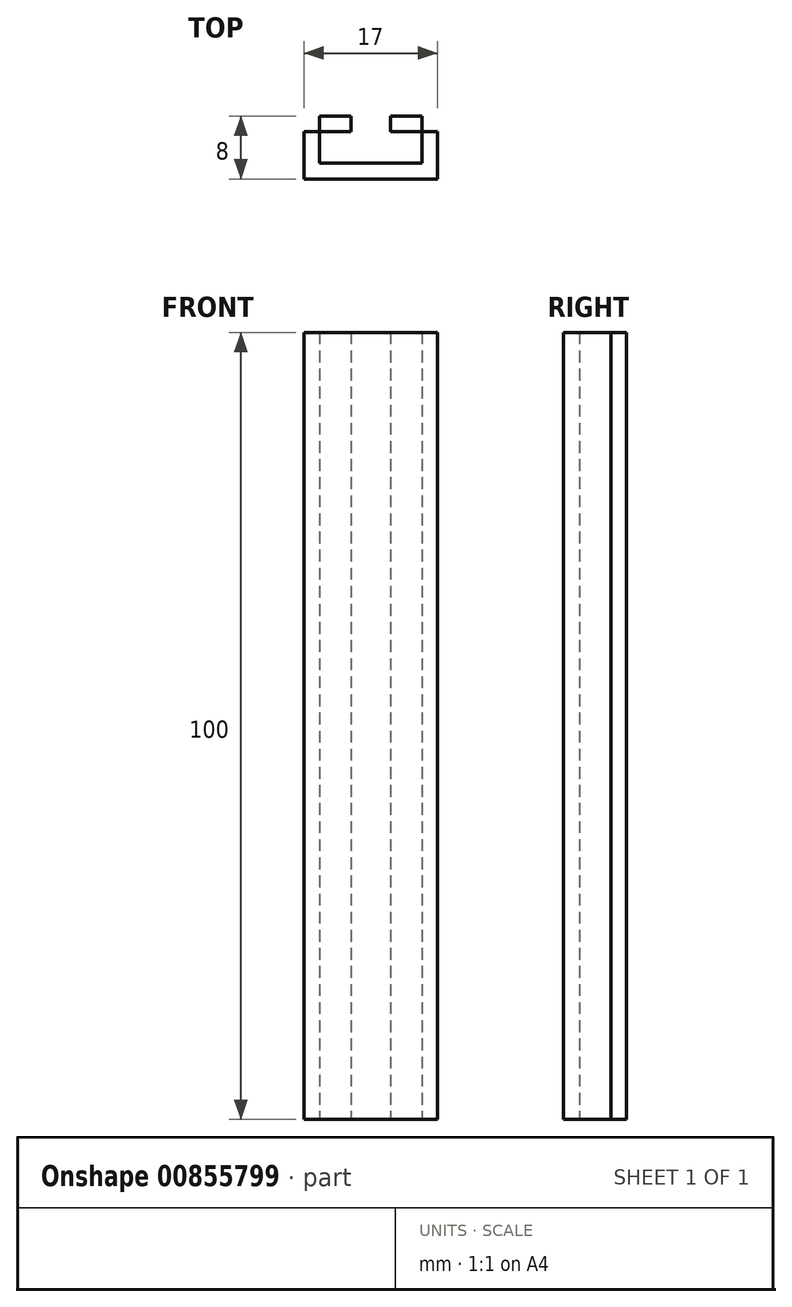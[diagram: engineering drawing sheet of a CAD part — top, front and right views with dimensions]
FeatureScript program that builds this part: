
annotation { "Feature Type Name" : "Feature", "Feature Type Description" : "" }
export const myFeature = defineFeature(function(context is Context, id is Id, definition is map)
    precondition{}
    {
        {
            var Q0;
            Q0=qCreatedBy(makeId("Top.planeOp"),FACE);
            var sketch = newSketch(context, id + "F0", { "sketchPlane" : qUnion([Q0])});
            skLineSegment(sketch, "E0.bottom", {"start": v(0, 0) * mm, "end": v(-8.5, 0) * mm});
            skLineSegment(sketch, "E0.top", {"start": v(0, 2) * mm, "end": v(-8.5, 2) * mm});
            skLineSegment(sketch, "E0.left", {"start": v(0, 0) * mm, "end": v(0, 2) * mm});
            skLineSegment(sketch, "E0.right", {"start": v(-8.5, 0) * mm, "end": v(-8.5, 2) * mm});
            skLineSegment(sketch, "E1.bottom", {"start": v(0, 0) * mm, "end": v(8.5, 0) * mm});
            skLineSegment(sketch, "E1.top", {"start": v(0, 2) * mm, "end": v(8.5, 2) * mm});
            skLineSegment(sketch, "E1.right", {"start": v(8.5, 0) * mm, "end": v(8.5, 2) * mm});
            skLineSegment(sketch, "E2.bottom", {"start": v(-8.5, 0) * mm, "end": v(-6.5, 0) * mm});
            skLineSegment(sketch, "E2.top", {"start": v(-8.5, 8) * mm, "end": v(-6.5, 8) * mm});
            skLineSegment(sketch, "E2.left", {"start": v(-8.5, 0) * mm, "end": v(-8.5, 8) * mm});
            skLineSegment(sketch, "E2.right", {"start": v(-6.5, 0) * mm, "end": v(-6.5, 8) * mm});
            skLineSegment(sketch, "E3.bottom", {"start": v(8.5, 0) * mm, "end": v(6.5, 0) * mm});
            skLineSegment(sketch, "E3.top", {"start": v(8.5, 8) * mm, "end": v(6.5, 8) * mm});
            skLineSegment(sketch, "E3.left", {"start": v(8.5, 0) * mm, "end": v(8.5, 8) * mm});
            skLineSegment(sketch, "E3.right", {"start": v(6.5, 0) * mm, "end": v(6.5, 8) * mm});
            skLineSegment(sketch, "E4.bottom", {"start": v(-8.5, 8) * mm, "end": v(-2.5, 8) * mm});
            skLineSegment(sketch, "E4.top", {"start": v(-8.5, 6) * mm, "end": v(-2.5, 6) * mm});
            skLineSegment(sketch, "E4.left", {"start": v(-8.5, 8) * mm, "end": v(-8.5, 6) * mm});
            skLineSegment(sketch, "E4.right", {"start": v(-2.5, 8) * mm, "end": v(-2.5, 6) * mm});
            skLineSegment(sketch, "E5.bottom", {"start": v(8.5, 8) * mm, "end": v(2.5, 8) * mm});
            skLineSegment(sketch, "E5.top", {"start": v(8.5, 6) * mm, "end": v(2.5, 6) * mm});
            skLineSegment(sketch, "E5.left", {"start": v(8.5, 8) * mm, "end": v(8.5, 6) * mm});
            skLineSegment(sketch, "E5.right", {"start": v(2.5, 8) * mm, "end": v(2.5, 6) * mm});
            skSolve(sketch);
        }
        {
            var Q0;
            {var subQ5=sQuery(id+"F0.wireOp",EDGE,"E4.right");Q0=makeQuery(id+"F0.imprint","IMPRINT",FACE,{"disambiguationData":[TD([[makeQuery(id+"F0.imprint","IMPRINT",EDGE,{"derivedFrom":subQ5}),-1.0]])]});}
            var Q1;
            {var subQ5=sQuery(id+"F0.wireOp",EDGE,"E4.left");Q1=makeQuery(id+"F0.imprint","IMPRINT",FACE,{"disambiguationData":[TD([[makeQuery(id+"F0.imprint","IMPRINT",EDGE,{"derivedFrom":subQ5}),1.0]])]});}
            var Q2;
            {var subQ0=sQuery(id+"F0.wireOp",EDGE,"E2.left");var subQ1=sQuery(id+"F0.wireOp",EDGE,"E0.top");var subQ2=makeQuery(id+"F0.imprint","INTERSECT",VERTEX,{"derivedFrom":[subQ1,subQ0]});Q2=makeQuery(id+"F0.imprint","IMPRINT",FACE,{"disambiguationData":[TD([[makeQuery(id+"F0.imprint","IMPRINT",EDGE,{"disambiguationData":[TD([[subQ2,1.0]])],"derivedFrom":subQ1}),-1.0]])]});}
            var Q3;
            {var subQ5=sQuery(id+"F0.wireOp",EDGE,"E2.bottom");Q3=makeQuery(id+"F0.imprint","IMPRINT",FACE,{"disambiguationData":[TD([[makeQuery(id+"F0.imprint","IMPRINT",EDGE,{"derivedFrom":subQ5}),1.0]])]});}
            var Q4;
            {var subQ0=sQuery(id+"F0.wireOp",EDGE,"E0.bottom");Q4=makeQuery(id+"F0.imprint","IMPRINT",FACE,{"disambiguationData":[TD([[makeQuery(id+"F0.imprint","IMPRINT",EDGE,{"derivedFrom":subQ0}),-1.0]])]});}
            var Q5;
            {var subQ0=sQuery(id+"F0.wireOp",EDGE,"E1.bottom");Q5=makeQuery(id+"F0.imprint","IMPRINT",FACE,{"disambiguationData":[TD([[makeQuery(id+"F0.imprint","IMPRINT",EDGE,{"derivedFrom":subQ0}),1.0]])]});}
            var Q6;
            {var subQ5=sQuery(id+"F0.wireOp",EDGE,"E3.bottom");Q6=makeQuery(id+"F0.imprint","IMPRINT",FACE,{"disambiguationData":[TD([[makeQuery(id+"F0.imprint","IMPRINT",EDGE,{"derivedFrom":subQ5}),-1.0]])]});}
            var Q7;
            {var subQ0=sQuery(id+"F0.wireOp",EDGE,"E3.left");var subQ1=sQuery(id+"F0.wireOp",EDGE,"E1.top");var subQ2=makeQuery(id+"F0.imprint","INTERSECT",VERTEX,{"derivedFrom":[subQ1,subQ0]});Q7=makeQuery(id+"F0.imprint","IMPRINT",FACE,{"disambiguationData":[TD([[makeQuery(id+"F0.imprint","IMPRINT",EDGE,{"disambiguationData":[TD([[subQ2,1.0]])],"derivedFrom":subQ1}),1.0]])]});}
            var Q8;
            {var subQ5=sQuery(id+"F0.wireOp",EDGE,"E5.left");Q8=makeQuery(id+"F0.imprint","IMPRINT",FACE,{"disambiguationData":[TD([[makeQuery(id+"F0.imprint","IMPRINT",EDGE,{"derivedFrom":subQ5}),-1.0]])]});}
            var Q9;
            {var subQ5=sQuery(id+"F0.wireOp",EDGE,"E5.right");Q9=makeQuery(id+"F0.imprint","IMPRINT",FACE,{"disambiguationData":[TD([[makeQuery(id+"F0.imprint","IMPRINT",EDGE,{"derivedFrom":subQ5}),1.0]])]});}
            extrude(context, id + "F1", {"entities" : qUnion([Q0, Q1, Q2, Q3, Q4, Q5, Q6, Q7, Q8, Q9]), "flatOperationType" : FlatOperationType.REMOVE, "endBound" : BoundingType.SYMMETRIC, "depth" : 100 * mm, "offsetDistance" : 25 * mm, "domain" : OperationDomain.MODEL});
        }
    });
